# Revit family: PRD_FrankeWS_ShwrMxrs_SelfClosingShowerMixer_F5SM2001-2003_V1
name_source: partatom
category: Plumbing Fixtures
revit_build: Autodesk Revit 2018 (Build: 20190510_1515(x64)
units: mm (PartAtom-declared; Revit-internal decimal feet)

## family parameters
Cut with Voids When Loaded = No
Host = Face
OmniClass Number = 23.45.05.14.99
OmniClass Title = Other Sanitary Washing Plumbing Fixtures
Part Type = Normal
Room Calculation Point = No
Round Connector Dimension = Use Diameter
Shared = No

## types (3) — shared parameters
AdditionalConnections = no
AdjustableFlowTime = yes
AssetType = Fixed
Category = Pr_40_20_87_78, Shower manual water supply sets
Circulation = no
CloseOffRating = 0.0 Pa
Color = Chrome
ConnectionWithPayWaterDispenser = not possible
Default Elevation = 850 mm  [stored 2.78871 ft]
DiameterNominal = 15.000 mm
DurationUnit = year
Features = For shower facilities. Connects to hot and cold water. All-metal construction, high-polished chromium-plated brass.
Finish = high-polished chromium-plated brass
FlowCoefficient = 0
FlowColdWater = 0.2 L/s
FlowHotWater = 0.2 L/s
FunctionalPrinciple = hydraulic self-closing
HygieneFlushing = no
IfcExportAs = IfcValveType
IfcExportType = MIXING
InletSize = G-1-2-B
Manufacturer = KWC Group AG
ManufacturerName = KWC Group AG
ManufacturerURL = www.kwc.com
Material = Brass
MaterialsBody = Brass
MaximumFlowTime = 35.00 seconds
MinimumFlowPressure = 0.50 bar
MinimumFlowTime = 5.00 seconds
MixerControl = Other
NBSDescription = Shower manual water supply sets
NBSReference = 45-35-70/335
NominalWidth = 223 mm  [stored 0.731627 ft]
OutletConnectionSize = 15 mm  [stored 0.0492126 ft]
PositionOfWaterConnection = from backside
ProductInformation = https://pim.kwc.com
ProtectiveShutdown = no
SoundInsulation = no
TapMaterial = PRD_AR_ChromatedBrass_HighPolished
TestPressure = 0.0 Pa
ThermalDisinfection = no
TypeOfMixing = with mixer
TypeOfMounting = Wall mounting
TypeOfOperation = manual operation
TypeOfShower = wall fitting
URL = www.kwc.com
Uniclass2015Code = Pr_40_20_87_78
Uniclass2015Title = Shower manual water supply sets
Uniclass2015Version = Products v1.10
ValveMechanism = Other
ValveOperation = Other
ValvePattern = ANGLED_2_PORT
Version = 1
WarrantyDurationUnit = year
zero-valued in all types: NominalHeight, NominalLength

## per-type parameters (varying)
| type | BIMObjectName | Description | GrossWeight | Model | ModelNumber | ModelReference | Name | NetWeight | OutletBottom | OutletTop | ShowerPipeDraining | ShowerPipeEmptying | VolumeFlowRate |
| F5SM2001 - 0.30 L/s, top outlet | PRD_AR_ShowerMixers_SelfClosingShowerMixer_F5SM2001 | F5S-Mix self-closing wall-mounted mixer DN 15 as single-mixer for wall mounting, for shower facilities. FRAMIC self-closing mixing cartridge, hydraulically controlled, low-maintenance and stagnation-free, with ceramic disc technology, self-closing, flow pressure-independent due to medium-separated design. Stepless adjustment of flow duration. With adjustable, turn-proof temperature stop. Connects to hot and cold water. Housing with outlet on top, G 3/4 B, for installation of bent outlet or surface-mounted shower pipe. All-metal construction, high-polished chromium-plated brass. With adjustable and turn-proof connections with backflow preventer and strainers, completely covered with depth-adjustable screw rosettes. | 4.30 kg | F5SM2001 | 2030032998 | F5SM2001 | F5 self-closing shower mixer F5SM2001 | 4.15 kg | No | Yes | no | No | 0.30 L/s at 3 bar |
| F5SM2002 - 0.30 L/s, top outlet with shower pipe draining | PRD_AR_ShowerMixers_SelfClosingShowerMixer_F5SM2002 | F5S-Mix self-closing wall-mounted mixer DN 15 as single-mixer for wall mounting, for shower facilities. FRAMIC self-closing mixing cartridge, hydraulically controlled, low-maintenance and stagnation-free, with ceramic disc technology, self-closing, flow pressure-independent due to medium-separated design. Stepless adjustment of flow duration. With adjustable, turn-proof temperature stop. Connects to hot and cold water. Housing with outlet on top, G 3/4 B, for installation of bent outlet or surface-mounted shower pipe. All-metal construction, high-polished chromium-plated brass. With adjustable and turn-proof connections with backflow preventer and strainers, completely covered with depth-adjustable screw rosettes. Version with automatic shower pipe draining. | 3.50 kg | F5SM2002 | 2030036685 | F5SM2002 | F5 self-closing shower mixer F5SM2002 | 3.30 kg | No | Yes | yes | Yes | 0.30 L/s at 3 bar |
| F5SM2003 - 0.20 L/s, bottom outlet | PRD_AR_ShowerMixers_SelfClosingShowerMixer_F5SM2003 | F5S-Mix self-closing wall-mounted mixer DN 15 as single-mixer for wall mounting, for shower facilities. FRAMIC self-closing mixing cartridge, hydraulically controlled, low-maintenance and stagnation-free, with ceramic disc technology, self-closing, flow pressure-independent due to medium-separated design. Stepless adjustment of flow duration. With adjustable, turn-proof temperature stop. Connects to hot and cold water. Housing with hand shower connection G 1/2 B. All-metal version, high-polished chromium-plated brass. With adjustable and turn-proof connections with backflow preventer and strainers, completely covered with depth-adjustable screw rosettes. | 4.30 kg | F5SM2003 | 2030036686 | F5SM2003 | F5 self-closing shower mixer F5SM2003 | 4.15 kg | Yes | No | no | No | 0.20 L/s at 3 bar |

note: [stored X ft] marks values corroborated as IEEE doubles in the binary element streams (Revit-internal decimal feet)

## geometry (parser evidence)
native form markers: Sweep x1
no freeform markers — native parametric forms only
